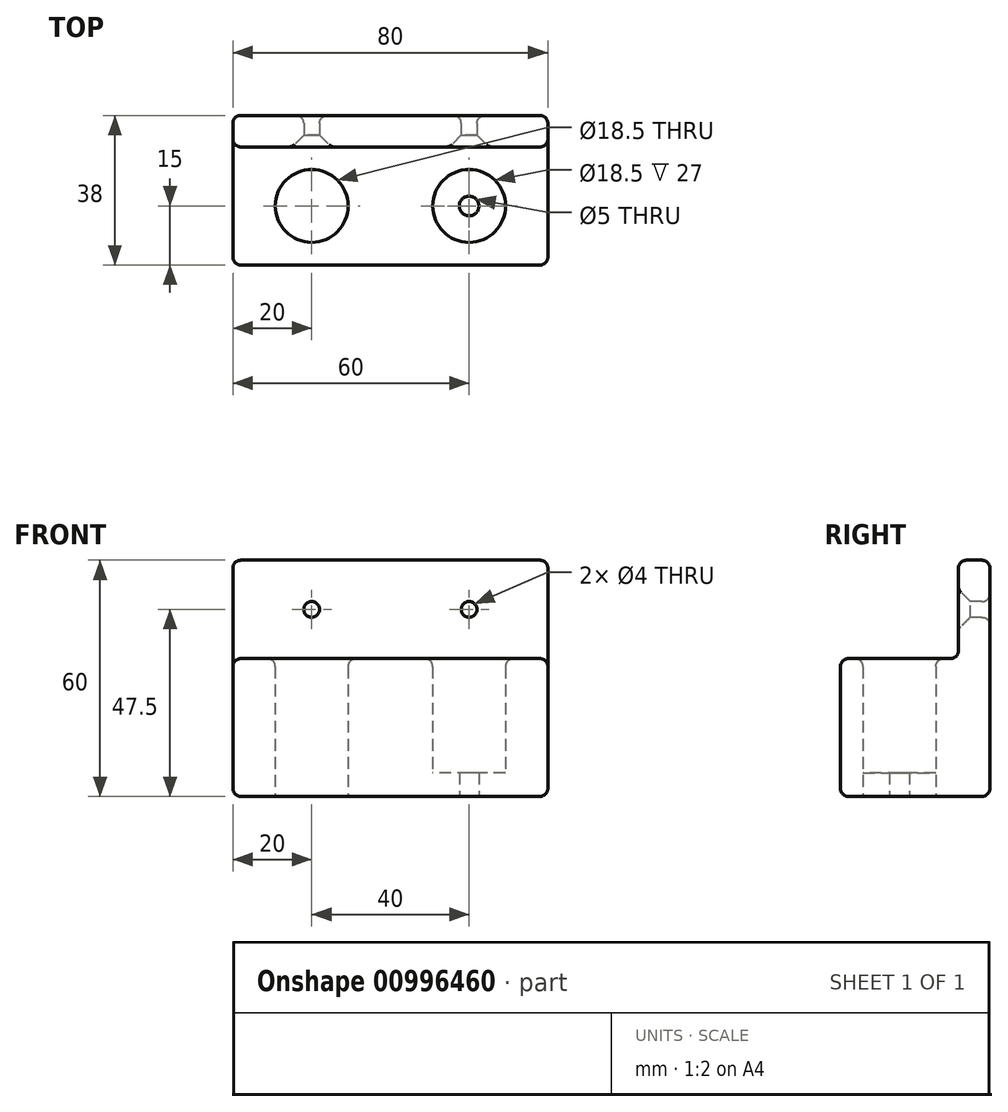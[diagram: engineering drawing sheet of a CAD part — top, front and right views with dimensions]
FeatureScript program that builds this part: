
annotation { "Feature Type Name" : "Feature", "Feature Type Description" : "" }
export const myFeature = defineFeature(function(context is Context, id is Id, definition is map)
    precondition{}
    {
        {
            var Q0;
            Q0=qCreatedBy(makeId("Top.planeOp"),FACE);
            var sketch = newSketch(context, id + "F0", { "sketchPlane" : qUnion([Q0])});
            skLineSegment(sketch, "E0.bottom", {"start": v(40, -15) * mm, "end": v(-40, -15) * mm});
            skLineSegment(sketch, "E0.top", {"start": v(40, 15) * mm, "end": v(-40, 15) * mm});
            skLineSegment(sketch, "E0.left", {"start": v(40, -15) * mm, "end": v(40, 15) * mm});
            skLineSegment(sketch, "E0.right", {"start": v(-40, -15) * mm, "end": v(-40, 15) * mm});
            skPoint(sketch, "E0.middle", {"position": v(0, 0) * mm});
            skLineSegment(sketch, "E1", {"start": v(-40, 0) * mm, "end": v(40, 0) * mm, "construction": true});
            skCircle(sketch, "E2", {"center": v(20, 0) * mm, "radius": 9.25 * mm});
            skCircle(sketch, "E3.MirrorC", {"center": v(-20, 0) * mm, "radius": 9.25 * mm});
            skLineSegment(sketch, "E4.top", {"start": v(40, 23) * mm, "end": v(-40, 23) * mm});
            skLineSegment(sketch, "E4.left", {"start": v(40, 15) * mm, "end": v(40, 23) * mm});
            skLineSegment(sketch, "E4.right", {"start": v(-40, 15) * mm, "end": v(-40, 23) * mm});
            skCircle(sketch, "E5", {"center": v(20, 0) * mm, "radius": 2.5 * mm});
            skCircle(sketch, "E6.MirrorC", {"center": v(-20, 0) * mm, "radius": 2.5 * mm});
            skLineSegment(sketch, "E7", {"start": v(20, 23) * mm, "end": v(20, -15) * mm, "construction": true});
            skSolve(sketch);
        }
        {
            var Q0;
            Q0=makeQuery(id+"F0.imprint","IMPRINT",FACE,{"disambiguationData":[TD([[makeQuery(id+"F0.imprint","IMPRINT",EDGE,{"derivedFrom":sQuery(id+"F0.wireOp",EDGE,"E0.top")}),-1.0]])]});
            extrude(context, id + "F1", {"entities" : qUnion([Q0]), "depth" : 60 * mm, "offsetDistance" : 25 * mm});
        }
        {
            var Q0;
            Q0 = qSketchRegion(id + "F0", true);
            var Q1;
            Q1=makeQuery(id+"F0.imprint","IMPRINT",FACE,{"disambiguationData":[TD([[makeQuery(id+"F0.imprint","IMPRINT",EDGE,{"derivedFrom":sQuery(id+"F0.wireOp",EDGE,"E0.bottom")}),-1.0]])]});
            extrude(context, id + "F2", {"entities" : qUnion([Q0, Q1]), "operationType" : NewBodyOperationType.ADD, "depth" : 35 * mm, "offsetDistance" : 25 * mm});
        }
        {
            var Q0;
            Q0=makeQuery(id+"F0.imprint","IMPRINT",FACE,{"disambiguationData":[TD([[makeQuery(id+"F0.imprint","IMPRINT",EDGE,{"derivedFrom":sQuery(id+"F0.wireOp",EDGE,"E2")}),1.0]])]});
            var Q1;
            Q1=makeQuery(id+"F0.imprint","IMPRINT",FACE,{"disambiguationData":[TD([[makeQuery(id+"F0.imprint","IMPRINT",EDGE,{"derivedFrom":sQuery(id+"F0.wireOp",EDGE,"E3.MirrorC")}),-1.0]])]});
            extrude(context, id + "F3", {"entities" : qUnion([Q0, Q1]), "operationType" : NewBodyOperationType.ADD, "depth" : 6 * mm, "offsetDistance" : 25 * mm});
        }
        {
            var Q0;
            Q0=makeQuery(id+"F1.opExtrude","SWEPT_FACE",FACE,{"disambiguationData":[OSD([sQuery(id+"F0.wireOp",EDGE,"E0.top")])]});
            var sketch = newSketch(context, id + "F4", { "sketchPlane" : qUnion([Q0])});
            skLineSegment(sketch, "E8", {"start": v(40, 47.5) * mm, "end": v(-40, 47.5) * mm, "construction": true});
            skLineSegment(sketch, "E9", {"start": v(20, 60) * mm, "end": v(20, 35) * mm, "construction": true});
            skLineSegment(sketch, "E10.MirrorCS", {"start": v(-20, 60) * mm, "end": v(-20, 35) * mm, "construction": true});
            skPoint(sketch, "E11", {"position": v(20, 47.5) * mm});
            skPoint(sketch, "E12", {"position": v(-20, 47.5) * mm});
            skSolve(sketch);
        }
        {
            var Q0;
            Q0=sQuery(id+"F4.wireOp",VERTEX,"E11");
            var Q1;
            Q1=sQuery(id+"F4.wireOp",VERTEX,"E12");
            var Q2;
            Q2=makeQuery(id+"F1.opExtrude","SWEPT_BODY",BODY,{"disambiguationData":[OSD([sQuery(id+"F0.wireOp",EDGE,"E0.top"),sQuery(id+"F0.wireOp",EDGE,"E4.top"),sQuery(id+"F0.wireOp",EDGE,"E4.left"),sQuery(id+"F0.wireOp",EDGE,"E4.right")])]});
            hole(context, id + "F5", {"style" : HoleStyle.C_SINK, "endStyle" : HoleEndStyle.THROUGH, "holeDiameter" : 4 * mm, "cSinkDiameter" : 10 * mm, "cSinkAngle" : 90 * degree, "majorDiameter" : 5 * mm, "isTappedThrough" : true, "tappedDepth" : 12 * mm, "tapClearance" : 3, "locations" : qUnion([Q0, Q1]), "scope" : qUnion([Q2])});
        }
        {
            var Q0;
            Q0=makeQuery(id+"F1.opExtrude","CAP_FACE",FACE,{"disambiguationData":[OSD([sQuery(id+"F0.wireOp",EDGE,"E0.top"),sQuery(id+"F0.wireOp",EDGE,"E4.top"),sQuery(id+"F0.wireOp",EDGE,"E4.left"),sQuery(id+"F0.wireOp",EDGE,"E4.right")])],"isStart":false});
            var Q1;
            Q1=makeQuery(id+"F2.opExtrude","SWEPT_FACE",FACE,{"disambiguationData":[OSD([sQuery(id+"F0.wireOp",EDGE,"E0.bottom")])]});
            var Q2;
            Q2=makeQuery(id+"F1.opExtrude","SWEPT_FACE",FACE,{"disambiguationData":[OSD([sQuery(id+"F0.wireOp",EDGE,"E0.top")])]});
            var Q3;
            Q3=makeQuery(id+"F1.opExtrude","SWEPT_FACE",FACE,{"disambiguationData":[OSD([sQuery(id+"F0.wireOp",EDGE,"E4.top")])]});
            var Q4;
            {var subQ0=sQuery(id+"F0.wireOp",EDGE,"E4.right");Q4=makeQuery(id+"F2.boolean.opBoolean","MERGE",FACE,{"derivedFrom":[makeQuery(id+"F1.opExtrude","SWEPT_FACE",FACE,{"disambiguationData":[OSD([subQ0])]}),makeQuery(id+"F2.opExtrude","SWEPT_FACE",FACE,{"disambiguationData":[OSD([sQuery(id+"F0.wireOp",EDGE,"E0.right"),subQ0])]})]});}
            var Q5;
            Q5=makeQuery(id+"F2.opExtrude","CAP_FACE",FACE,{"disambiguationData":[OSD([sQuery(id+"F0.wireOp",EDGE,"E0.bottom"),sQuery(id+"F0.wireOp",EDGE,"E0.left"),sQuery(id+"F0.wireOp",EDGE,"E0.right"),sQuery(id+"F0.wireOp",EDGE,"E2"),sQuery(id+"F0.wireOp",EDGE,"E3.MirrorC"),sQuery(id+"F0.wireOp",EDGE,"E4.top"),sQuery(id+"F0.wireOp",EDGE,"E4.left"),sQuery(id+"F0.wireOp",EDGE,"E4.right")])],"isStart":false});
            var Q6;
            {var subQ0=sQuery(id+"F0.wireOp",EDGE,"E4.left");Q6=makeQuery(id+"F2.boolean.opBoolean","MERGE",FACE,{"derivedFrom":[makeQuery(id+"F1.opExtrude","SWEPT_FACE",FACE,{"disambiguationData":[OSD([subQ0])]}),makeQuery(id+"F2.opExtrude","SWEPT_FACE",FACE,{"disambiguationData":[OSD([sQuery(id+"F0.wireOp",EDGE,"E0.left"),subQ0])]})]});}
            fillet(context, id + "F6", {"entities" : qUnion([Q0, Q1, Q2, Q3, Q4, Q5, Q6]), "radius" : 2 * mm, "tangentPropagation" : true, "allowEdgeOverflow" : false});
        }
    });
